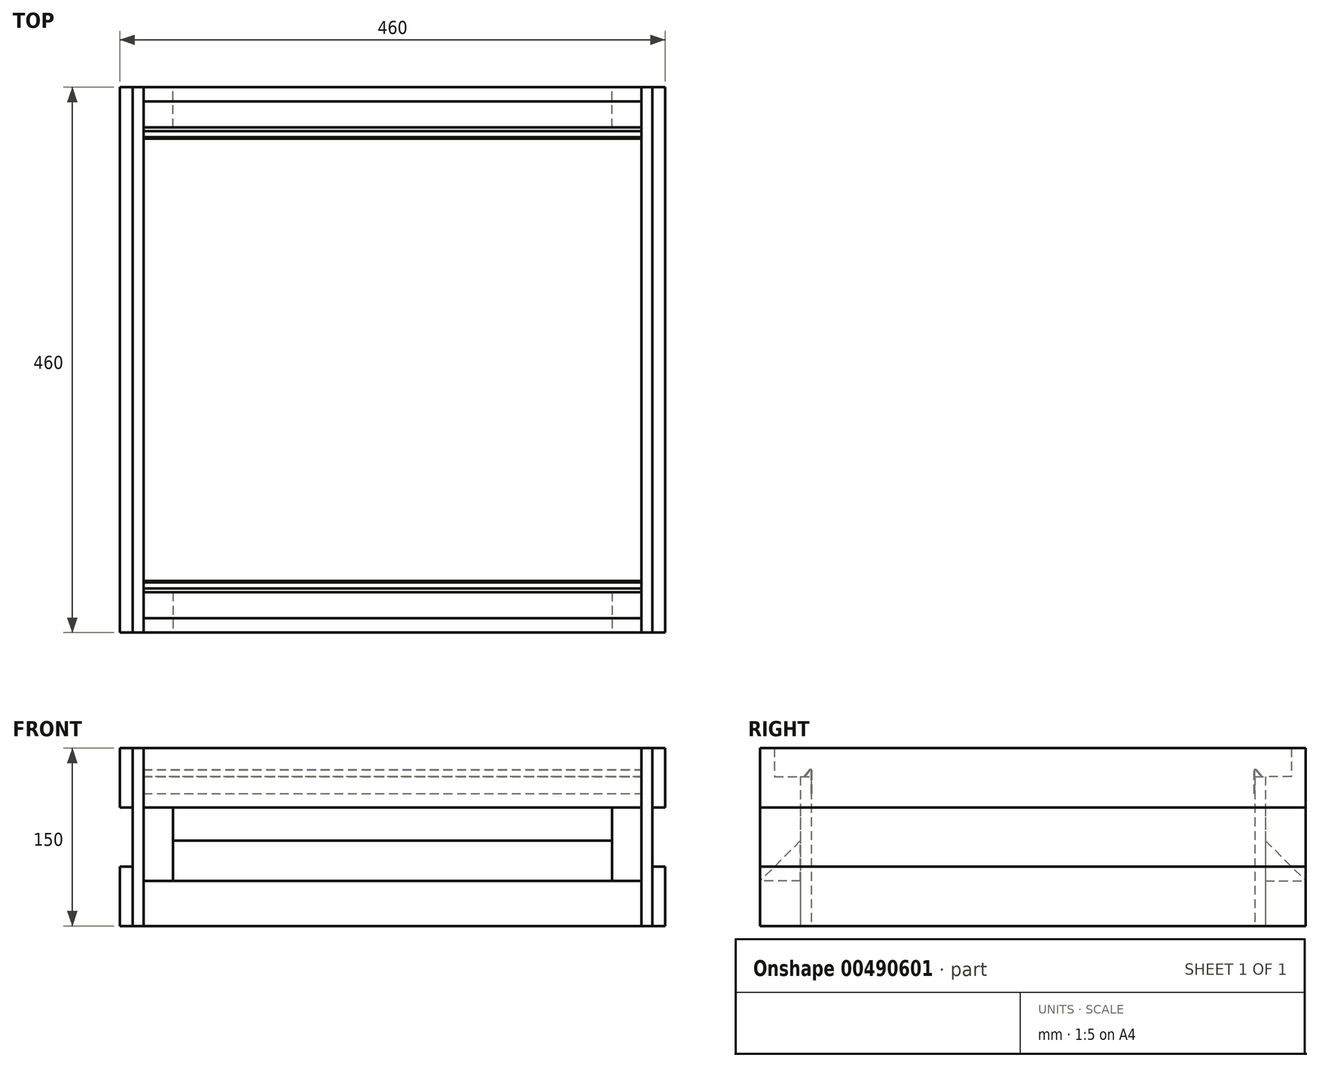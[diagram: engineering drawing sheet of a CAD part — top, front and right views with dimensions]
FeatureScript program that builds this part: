
annotation { "Feature Type Name" : "Feature", "Feature Type Description" : "" }
export const myFeature = defineFeature(function(context is Context, id is Id, definition is map)
    precondition{}
    {
        {
            var Q0;
            Q0=qCreatedBy(makeId("Right.planeOp"),FACE);
            var sketch = newSketch(context, id + "F0", { "sketchPlane" : qUnion([Q0])});
            skLineSegment(sketch, "E0", {"start": v(231.18, 0) * mm, "end": v(231.18, 279.77) * mm, "construction": true});
            skLineSegment(sketch, "E1.right", {"start": v(44.18, 288.91) * mm, "end": v(44.18, 162.91) * mm});
            skLineSegment(sketch, "E2.MirrorCS", {"start": v(418.18, 288.91) * mm, "end": v(418.18, 162.91) * mm});
            skLineSegment(sketch, "E3", {"start": v(35.18, 288.91) * mm, "end": v(35.18, 162.91) * mm});
            skLineSegment(sketch, "E4", {"start": v(427.18, 288.91) * mm, "end": v(427.18, 162.91) * mm});
            skPoint(sketch, "E5.orphan", {"position": v(26.18, 290.5) * mm});
            skPoint(sketch, "E6.MirrorCS.start.orphan", {"position": v(436.18, 290.5) * mm});
            skPoint(sketch, "E1.bottom.end.orphan", {"position": v(44.18, 290.5) * mm});
            skPoint(sketch, "E1.bottom.start.orphan", {"position": v(35.18, 290.5) * mm});
            skPoint(sketch, "E7.MirrorCS.end.orphan", {"position": v(418.18, 290.5) * mm});
            skPoint(sketch, "E7.MirrorCS.start.orphan", {"position": v(427.18, 290.5) * mm});
            skLineSegment(sketch, "E8", {"start": v(35.18, 288.91) * mm, "end": v(44.18, 288.91) * mm});
            skLineSegment(sketch, "E9.trimOffspring", {"start": v(418.18, 288.91) * mm, "end": v(427.18, 288.91) * mm});
            skLineSegment(sketch, "E10.0", {"start": v(35.18, 162.91) * mm, "end": v(44.18, 162.91) * mm});
            skLineSegment(sketch, "E11.0", {"start": v(427.18, 162.91) * mm, "end": v(418.18, 162.91) * mm});
            skPoint(sketch, "E12.orphan", {"position": v(418.18, 270.91) * mm});
            skSolve(sketch);
        }
        {
            var Q0;
            Q0=qSketchRegion(id+"F0",true);
            extrude(context, id + "F1", {"entities" : qUnion([Q0]), "depth" : 420 * mm, "symmetric" : true});
        }
        {
            var Q0;
            Q0=qCreatedBy(makeId("Right.planeOp"),FACE);
            var sketch = newSketch(context, id + "F2", { "sketchPlane" : qUnion([Q0])});
            skLineSegment(sketch, "E13", {"start": v(1.18, 162.91) * mm, "end": v(1.18, 200.91) * mm});
            skLineSegment(sketch, "E14", {"start": v(231.18, 0) * mm, "end": v(231.18, 279.77) * mm, "construction": true});
            skLineSegment(sketch, "E15", {"start": v(1.18, 312.91) * mm, "end": v(13.18, 312.91) * mm});
            skLineSegment(sketch, "E16", {"start": v(13.18, 312.91) * mm, "end": v(13.18, 288.91) * mm});
            skLineSegment(sketch, "E17", {"start": v(35.18, 262.91) * mm, "end": v(1.18, 262.91) * mm});
            skLineSegment(sketch, "E18", {"start": v(1.18, 162.91) * mm, "end": v(35.18, 162.91) * mm});
            skLineSegment(sketch, "E19", {"start": v(35.18, 200.91) * mm, "end": v(1.18, 200.91) * mm});
            skLineSegment(sketch, "E20.trimOffspring", {"start": v(1.18, 262.91) * mm, "end": v(1.18, 312.91) * mm});
            skLineSegment(sketch, "E21.0", {"start": v(13.18, 288.91) * mm, "end": v(35.18, 288.91) * mm});
            skPoint(sketch, "E22.orphan", {"position": v(35.18, 288.91) * mm});
            skLineSegment(sketch, "E23.0", {"start": v(35.18, 288.91) * mm, "end": v(35.18, 262.91) * mm});
            skPoint(sketch, "E24.orphan", {"position": v(39.86, 200.91) * mm});
            skLineSegment(sketch, "E25.trimOffspring", {"start": v(35.18, 200.91) * mm, "end": v(35.18, 162.91) * mm});
            skPoint(sketch, "E26.orphan", {"position": v(35.18, 162.91) * mm});
            skLineSegment(sketch, "E27.MirrorCS", {"start": v(461.18, 312.91) * mm, "end": v(449.18, 312.91) * mm});
            skLineSegment(sketch, "E28.MirrorCS", {"start": v(449.18, 288.91) * mm, "end": v(427.18, 288.91) * mm});
            skLineSegment(sketch, "E29.MirrorCS", {"start": v(427.18, 288.91) * mm, "end": v(427.18, 262.91) * mm});
            skLineSegment(sketch, "E30.MirrorCS", {"start": v(461.18, 162.91) * mm, "end": v(461.18, 200.91) * mm});
            skPoint(sketch, "E31.MirrorP", {"position": v(427.18, 288.91) * mm});
            skLineSegment(sketch, "E32.MirrorCS", {"start": v(427.18, 262.91) * mm, "end": v(461.18, 262.91) * mm});
            skPoint(sketch, "E33.MirrorP", {"position": v(422.5, 200.91) * mm});
            skLineSegment(sketch, "E34.MirrorCS", {"start": v(461.18, 262.91) * mm, "end": v(461.18, 312.91) * mm});
            skLineSegment(sketch, "E35.MirrorCS", {"start": v(449.18, 312.91) * mm, "end": v(449.18, 288.91) * mm});
            skPoint(sketch, "E36.MirrorP", {"position": v(427.18, 162.91) * mm});
            skLineSegment(sketch, "E37.MirrorCS", {"start": v(427.18, 200.91) * mm, "end": v(461.18, 200.91) * mm});
            skLineSegment(sketch, "E38.MirrorCS", {"start": v(427.18, 200.91) * mm, "end": v(427.18, 162.91) * mm});
            skLineSegment(sketch, "E39.MirrorCS", {"start": v(461.18, 162.91) * mm, "end": v(427.18, 162.91) * mm});
            skSolve(sketch);
        }
        {
            var Q0;
            Q0=qSketchRegion(id+"F2",true);
            extrude(context, id + "F3", {"entities" : qUnion([Q0]), "depth" : 420 * mm, "symmetric" : true});
        }
        {
            var Q0;
            Q0=makeQuery(id+"F1.opExtrude","CAP_FACE",FACE,{"disambiguationData":[OSD([sQuery(id+"F0.wireOp",EDGE,"E1.right"),sQuery(id+"F0.wireOp",EDGE,"E3"),sQuery(id+"F0.wireOp",EDGE,"QR00Nk12-EYIH-hDG3-dkOs-eiUDFboGELUt"),sQuery(id+"F0.wireOp",EDGE,"E8"),sQuery(id+"F0.wireOp",EDGE,"vDRYB3Tc-J4Gi-Wg77-MHAF-t7Dz2F66pPay"),sQuery(id+"F0.wireOp",EDGE,"hcTop7U9-e987-0MDV-DPT9-K6rQsRRchhsj")])],"isStart":false});
            var sketch = newSketch(context, id + "F4", { "sketchPlane" : qUnion([Q0])});
            skLineSegment(sketch, "E40.1", {"start": v(44.18, 293.88) * mm, "end": v(44.18, 274.52) * mm});
            skLineSegment(sketch, "E41", {"start": v(38.68, 288.92) * mm, "end": v(43.12, 294.27) * mm});
            skArc(sketch, "E42.filletArc", {"start": v(44.18, 293.88) * mm, "mid": v(43.78, 294.45) * mm, "end": v(43.12, 294.27) * mm});
            skLineSegment(sketch, "E43.0", {"start": v(44.73, 293.88) * mm, "end": v(44.73, 274.52) * mm});
            skArc(sketch, "E43.1", {"start": v(44.73, 293.88) * mm, "mid": v(44.49, 294.59) * mm, "end": v(43.86, 295) * mm});
            skLineSegment(sketch, "E43.2", {"start": v(38.25, 289.27) * mm, "end": v(42.7, 294.62) * mm});
            skLineSegment(sketch, "E44", {"start": v(44.73, 274.52) * mm, "end": v(44.18, 274.52) * mm});
            skLineSegment(sketch, "E45", {"start": v(38.25, 289.27) * mm, "end": v(38.68, 288.92) * mm});
            skLineSegment(sketch, "E46", {"start": v(43.3, 295) * mm, "end": v(43.86, 295) * mm});
            skPoint(sketch, "E46.startSnap0", {"position": v(43.86, 295) * mm});
            skArc(sketch, "E47.trimOffspring", {"start": v(43.3, 295) * mm, "mid": v(42.97, 294.86) * mm, "end": v(42.7, 294.62) * mm});
            skPoint(sketch, "E48.orphan", {"position": v(42.7, 295) * mm});
            skLineSegment(sketch, "E49", {"start": v(44.18, 162.91) * mm, "end": v(418.18, 162.91) * mm, "construction": true});
            skLineSegment(sketch, "E50", {"start": v(231.18, 162.91) * mm, "end": v(231.18, 199.9) * mm, "construction": true});
            skLineSegment(sketch, "E51.MirrorCS", {"start": v(424.1, 289.27) * mm, "end": v(423.68, 288.92) * mm, "construction": true});
            skArc(sketch, "E52.MirrorCS", {"start": v(418.18, 293.88) * mm, "mid": v(418.58, 294.45) * mm, "end": v(419.24, 294.27) * mm, "construction": true});
            skLineSegment(sketch, "E53.MirrorCS", {"start": v(419.06, 295) * mm, "end": v(418.5, 295) * mm, "construction": true});
            skLineSegment(sketch, "E54.MirrorCS", {"start": v(423.68, 288.92) * mm, "end": v(419.24, 294.27) * mm, "construction": true});
            skArc(sketch, "E55.MirrorCS", {"start": v(419.06, 295) * mm, "mid": v(419.4, 294.86) * mm, "end": v(419.66, 294.62) * mm, "construction": true});
            skArc(sketch, "E56.MirrorCS", {"start": v(417.63, 293.88) * mm, "mid": v(417.87, 294.59) * mm, "end": v(418.5, 295) * mm, "construction": true});
            skLineSegment(sketch, "E57.MirrorCS", {"start": v(424.1, 289.27) * mm, "end": v(419.66, 294.62) * mm, "construction": true});
            skLineSegment(sketch, "E58.MirrorCS", {"start": v(418.18, 293.88) * mm, "end": v(418.18, 274.52) * mm, "construction": true});
            skLineSegment(sketch, "E59.MirrorCS", {"start": v(417.63, 293.88) * mm, "end": v(417.63, 274.52) * mm, "construction": true});
            skLineSegment(sketch, "E60.MirrorCS", {"start": v(417.63, 274.52) * mm, "end": v(418.18, 274.52) * mm, "construction": true});
            skPoint(sketch, "E61.MirrorP", {"position": v(418.5, 295) * mm});
            skPoint(sketch, "E62.MirrorP", {"position": v(419.66, 295) * mm});
            skSolve(sketch);
        }
        {
            var Q0;
            Q0=qSketchRegion(id+"F4",true);
            var Q1;
            Q1=makeQuery(id+"F1.opExtrude","CAP_FACE",FACE,{"disambiguationData":[OSD([sQuery(id+"F0.wireOp",EDGE,"E1.right"),sQuery(id+"F0.wireOp",EDGE,"E3"),sQuery(id+"F0.wireOp",EDGE,"QR00Nk12-EYIH-hDG3-dkOs-eiUDFboGELUt"),sQuery(id+"F0.wireOp",EDGE,"E8"),sQuery(id+"F0.wireOp",EDGE,"vDRYB3Tc-J4Gi-Wg77-MHAF-t7Dz2F66pPay"),sQuery(id+"F0.wireOp",EDGE,"hcTop7U9-e987-0MDV-DPT9-K6rQsRRchhsj")])],"isStart":true});
            extrude(context, id + "F5", {"entities" : qUnion([Q0]), "endBound" : BoundingType.UP_TO_SURFACE, "oppositeDirection" : true, "endBoundEntityFace" : qUnion([Q1]), "depth" : 25.4 * mm});
        }
        {
            var Q0;
            Q0=makeQuery(id+"F1.opExtrude","SWEPT_FACE",FACE,{"disambiguationData":[OSD([sQuery(id+"F0.wireOp",EDGE,"E1.right")])]});
            var Q1;
            Q1=makeQuery(id+"F1.opExtrude","SWEPT_FACE",FACE,{"disambiguationData":[OSD([sQuery(id+"F0.wireOp",EDGE,"E2.MirrorCS")])]});
            cPlane(context, id + "F6", {"entities" : qUnion([Q0, Q1]), "cplaneType" : CPlaneType.MID_PLANE, "offset" : 25 * mm, "width" : 150 * mm, "height" : 150 * mm});
        }
        {
            var Q0;
            Q0=makeQuery(id+"F5.opExtrude","SWEPT_BODY",BODY,{"disambiguationData":[OSD([sQuery(id+"F4.wireOp",EDGE,"E40.1"),sQuery(id+"F4.wireOp",EDGE,"E41"),sQuery(id+"F4.wireOp",EDGE,"E42.filletArc"),sQuery(id+"F4.wireOp",EDGE,"E43.0"),sQuery(id+"F4.wireOp",EDGE,"E43.1"),sQuery(id+"F4.wireOp",EDGE,"E43.2"),sQuery(id+"F4.wireOp",EDGE,"E44"),sQuery(id+"F4.wireOp",EDGE,"E45"),sQuery(id+"F4.wireOp",EDGE,"E46"),sQuery(id+"F4.wireOp",EDGE,"E47.trimOffspring")])]});
            var Q1;
            Q1=qCreatedBy(id+"F6.planeOp",FACE);
            mirror(context, id + "F7", {"entities" : qUnion([Q0]), "mirrorPlane" : qUnion([Q1])});
        }
        {
            var Q0;
            Q0=makeQuery(id+"F3.opExtrude","CAP_FACE",FACE,{"disambiguationData":[OSD([sQuery(id+"F2.wireOp",EDGE,"E15"),sQuery(id+"F2.wireOp",EDGE,"E16"),sQuery(id+"F2.wireOp",EDGE,"E17"),sQuery(id+"F2.wireOp",EDGE,"E20.trimOffspring"),sQuery(id+"F2.wireOp",EDGE,"82fd9273-c707-4ff1-94b9-1b56f909c31e.0"),sQuery(id+"F2.wireOp",EDGE,"ba24a14a-bd92-40fe-843e-f5e0caba9491.0"),sQuery(id+"F2.wireOp",EDGE,"US8iAf4N-KQBx-rcmz-rff0-gODSU24NLPX8"),sQuery(id+"F2.wireOp",EDGE,"IBiT1izF-VUWa-IY42-BiTY-wa7s07OdXrZS")])],"isStart":false});
            var sketch = newSketch(context, id + "F8", { "sketchPlane" : qUnion([Q0])});
            skLineSegment(sketch, "E63.0", {"start": v(1.18, 162.91) * mm, "end": v(461.18, 162.91) * mm});
            skLineSegment(sketch, "E64.0", {"start": v(1.18, 312.91) * mm, "end": v(13.18, 312.91) * mm});
            skLineSegment(sketch, "E65", {"start": v(1.18, 312.91) * mm, "end": v(1.18, 162.91) * mm});
            skLineSegment(sketch, "E66", {"start": v(13.18, 312.91) * mm, "end": v(461.18, 312.91) * mm});
            skLineSegment(sketch, "E67.0", {"start": v(461.18, 162.91) * mm, "end": v(461.18, 312.91) * mm});
            skSolve(sketch);
        }
        {
            var Q0;
            Q0=qSketchRegion(id+"F8",true);
            extrude(context, id + "F9", {"entities" : qUnion([Q0]), "depth" : 9 * mm});
        }
        {
            var Q0;
            Q0=makeQuery(id+"F9.opExtrude","SWEPT_FACE",FACE,{"disambiguationData":[OSD([sQuery(id+"F8.wireOp",EDGE,"E65")])]});
            var sketch = newSketch(context, id + "F10", { "sketchPlane" : qUnion([Q0])});
            skLineSegment(sketch, "E68", {"start": v(230, 262.91) * mm, "end": v(230, 312.91) * mm});
            skLineSegment(sketch, "E69.0", {"start": v(230, 312.91) * mm, "end": v(219, 312.91) * mm});
            skPoint(sketch, "E70.orphan", {"position": v(-210, 312.91) * mm});
            skLineSegment(sketch, "E71", {"start": v(219, 237.91) * mm, "end": v(259.35, 237.91) * mm, "construction": true});
            skLineSegment(sketch, "E72", {"start": v(230, 262.91) * mm, "end": v(219, 262.91) * mm});
            skLineSegment(sketch, "E73.0", {"start": v(219, 312.91) * mm, "end": v(219, 262.91) * mm});
            skPoint(sketch, "E74.orphan", {"position": v(219, 162.91) * mm});
            skLineSegment(sketch, "E75.MirrorCS", {"start": v(230, 162.91) * mm, "end": v(219, 162.91) * mm});
            skLineSegment(sketch, "E76.MirrorCS", {"start": v(230, 212.91) * mm, "end": v(219, 212.91) * mm});
            skLineSegment(sketch, "E77.MirrorCS", {"start": v(230, 212.91) * mm, "end": v(230, 162.91) * mm});
            skLineSegment(sketch, "E78.MirrorCS", {"start": v(219, 162.91) * mm, "end": v(219, 212.91) * mm});
            skSolve(sketch);
        }
        {
            var Q0;
            Q0=qSketchRegion(id+"F10",true);
            var Q1;
            Q1=makeQuery(id+"F9.opExtrude","SWEPT_FACE",FACE,{"disambiguationData":[OSD([sQuery(id+"F8.wireOp",EDGE,"E67.0")])]});
            var Q2;
            Q2=makeQuery(id+"F9.opExtrude","SWEPT_FACE",FACE,{"disambiguationData":[OSD([sQuery(id+"F8.wireOp",EDGE,"fd9dc453-e4fe-45ab-abac-2d0b98b48e28.1")])]});
            extrude(context, id + "F11", {"entities" : qUnion([Q0]), "endBound" : BoundingType.UP_TO_SURFACE, "oppositeDirection" : true, "endBoundEntityFace" : qUnion([Q1]), "depth" : 456.18 * mm});
        }
        {
            var Q0;
            Q0=makeQuery(id+"F9.opExtrude","CAP_FACE",FACE,{"disambiguationData":[OSD([sQuery(id+"F8.wireOp",EDGE,"E63.0"),sQuery(id+"F8.wireOp",EDGE,"E64.0"),sQuery(id+"F8.wireOp",EDGE,"E65"),sQuery(id+"F8.wireOp",EDGE,"E66"),sQuery(id+"F8.wireOp",EDGE,"E67.0")])],"isStart":true});
            var sketch = newSketch(context, id + "F12", { "sketchPlane" : qUnion([Q0])});
            skLineSegment(sketch, "E79.1", {"start": v(-35.18, 263.52) * mm, "end": v(-35.18, 200.91) * mm});
            skLineSegment(sketch, "E80.2", {"start": v(-35.18, 262.91) * mm, "end": v(-1.18, 262.91) * mm});
            skLineSegment(sketch, "E80.3", {"start": v(-35.18, 200.91) * mm, "end": v(-1.18, 200.91) * mm});
            skLineSegment(sketch, "E81.0", {"start": v(-1.18, 262.91) * mm, "end": v(-1.18, 200.91) * mm});
            skPoint(sketch, "E82.orphan", {"position": v(-35.18, 288.91) * mm});
            skPoint(sketch, "E83.orphan", {"position": v(-1.18, 262.91) * mm});
            skPoint(sketch, "E84.orphan", {"position": v(-35.18, 162.91) * mm});
            skPoint(sketch, "E85.orphan", {"position": v(-1.18, 200.91) * mm});
            skLineSegment(sketch, "E86", {"start": v(-231.18, 143.1) * mm, "end": v(-231.18, 162.91) * mm, "construction": true});
            skPoint(sketch, "E87.MirrorP", {"position": v(-461.18, 200.91) * mm});
            skLineSegment(sketch, "E88.MirrorCS", {"start": v(-427.18, 200.91) * mm, "end": v(-461.18, 200.91) * mm});
            skLineSegment(sketch, "E89.MirrorCS", {"start": v(-427.18, 262.91) * mm, "end": v(-461.18, 262.91) * mm});
            skPoint(sketch, "E90.MirrorP", {"position": v(-461.18, 262.91) * mm});
            skLineSegment(sketch, "E91.MirrorCS", {"start": v(-427.18, 263.52) * mm, "end": v(-427.18, 200.91) * mm});
            skLineSegment(sketch, "E92.MirrorCS", {"start": v(-461.18, 262.91) * mm, "end": v(-461.18, 200.91) * mm});
            skPoint(sketch, "E93.MirrorP", {"position": v(-427.18, 288.91) * mm});
            skPoint(sketch, "E94.MirrorP", {"position": v(-427.18, 162.91) * mm});
            skSolve(sketch);
        }
        {
            var Q0;
            Q0=qSketchRegion(id+"F12",true);
            extrude(context, id + "F13", {"entities" : qUnion([Q0]), "offsetDistance" : 25 * mm, "depth" : 25 * mm});
        }
        {
            var Q0;
            Q0=makeQuery(id+"F9.opExtrude","SWEPT_BODY",BODY,{"disambiguationData":[OSD([sQuery(id+"F8.wireOp",EDGE,"E63.0"),sQuery(id+"F8.wireOp",EDGE,"E64.0"),sQuery(id+"F8.wireOp",EDGE,"E65"),sQuery(id+"F8.wireOp",EDGE,"E66"),sQuery(id+"F8.wireOp",EDGE,"E67.0")])]});
            var Q1;
            Q1=makeQuery(id+"F11.opExtrude","SWEPT_BODY",BODY,{"disambiguationData":[OSD([sQuery(id+"F10.wireOp",EDGE,"E75.MirrorCS"),sQuery(id+"F10.wireOp",EDGE,"E76.MirrorCS"),sQuery(id+"F10.wireOp",EDGE,"E77.MirrorCS"),sQuery(id+"F10.wireOp",EDGE,"E78.MirrorCS")])]});
            var Q2;
            Q2=makeQuery(id+"F11.opExtrude","SWEPT_BODY",BODY,{"disambiguationData":[OSD([sQuery(id+"F10.wireOp",EDGE,"E68"),sQuery(id+"F10.wireOp",EDGE,"E69.0"),sQuery(id+"F10.wireOp",EDGE,"E72"),sQuery(id+"F10.wireOp",EDGE,"E73.0")])]});
            var Q3;
            Q3=makeQuery(id+"F13.opExtrude","SWEPT_BODY",BODY,{"disambiguationData":[OSD([sQuery(id+"F12.wireOp",EDGE,"E79.1"),sQuery(id+"F12.wireOp",EDGE,"E80.2"),sQuery(id+"F12.wireOp",EDGE,"E80.3"),sQuery(id+"F12.wireOp",EDGE,"E81.0")])]});
            var Q4;
            Q4=makeQuery(id+"F13.opExtrude","SWEPT_BODY",BODY,{"disambiguationData":[OSD([sQuery(id+"F12.wireOp",EDGE,"E88.MirrorCS"),sQuery(id+"F12.wireOp",EDGE,"E89.MirrorCS"),sQuery(id+"F12.wireOp",EDGE,"E91.MirrorCS"),sQuery(id+"F12.wireOp",EDGE,"E92.MirrorCS")])]});
            var Q5;
            Q5=qCreatedBy(makeId("Right.planeOp"),FACE);
            mirror(context, id + "F14", {"entities" : qUnion([Q0, Q1, Q2, Q3, Q4]), "mirrorPlane" : qUnion([Q5])});
        }
        {
            var Q0;
            Q0=makeQuery(id+"F13.opExtrude","CAP_FACE",FACE,{"disambiguationData":[OSD([sQuery(id+"F12.wireOp",EDGE,"E79.1"),sQuery(id+"F12.wireOp",EDGE,"E80.2"),sQuery(id+"F12.wireOp",EDGE,"E80.3"),sQuery(id+"F12.wireOp",EDGE,"E81.0")])],"isStart":false});
            var sketch = newSketch(context, id + "F15", { "sketchPlane" : qUnion([Q0])});
            skLineSegment(sketch, "E95.0", {"start": v(-35.18, 200.91) * mm, "end": v(-1.18, 200.91) * mm});
            skLineSegment(sketch, "E96", {"start": v(-35.18, 200.91) * mm, "end": v(-35.18, 234.91) * mm});
            skLineSegment(sketch, "E97", {"start": v(-1.18, 200.91) * mm, "end": v(-35.18, 234.91) * mm});
            skLineSegment(sketch, "E98.MirrorCS", {"start": v(-427.18, 200.91) * mm, "end": v(-427.18, 234.91) * mm});
            skLineSegment(sketch, "E99.MirrorCS", {"start": v(-461.18, 200.91) * mm, "end": v(-427.18, 234.91) * mm});
            skLineSegment(sketch, "E100.MirrorCS", {"start": v(-427.18, 200.91) * mm, "end": v(-461.18, 200.91) * mm});
            skSolve(sketch);
        }
        {
            var Q0;
            Q0 = qSketchRegion(id + "F15", true);
            var Q1;
            Q1=makeQuery(id+"F14.opPattern","COPY",FACE,{"derivedFrom":makeQuery(id+"F13.opExtrude","CAP_FACE",FACE,{"disambiguationData":[OSD([sQuery(id+"F12.wireOp",EDGE,"E79.1"),sQuery(id+"F12.wireOp",EDGE,"E80.2"),sQuery(id+"F12.wireOp",EDGE,"E80.3"),sQuery(id+"F12.wireOp",EDGE,"E81.0")])],"isStart":false}),"instanceName":"1"});
            extrude(context, id + "F16", {"entities" : qUnion([Q0]), "endBound" : BoundingType.UP_TO_SURFACE, "depth" : 25 * mm, "endBoundEntityFace" : qUnion([Q1]), "offsetDistance" : 25 * mm});
        }
    });
